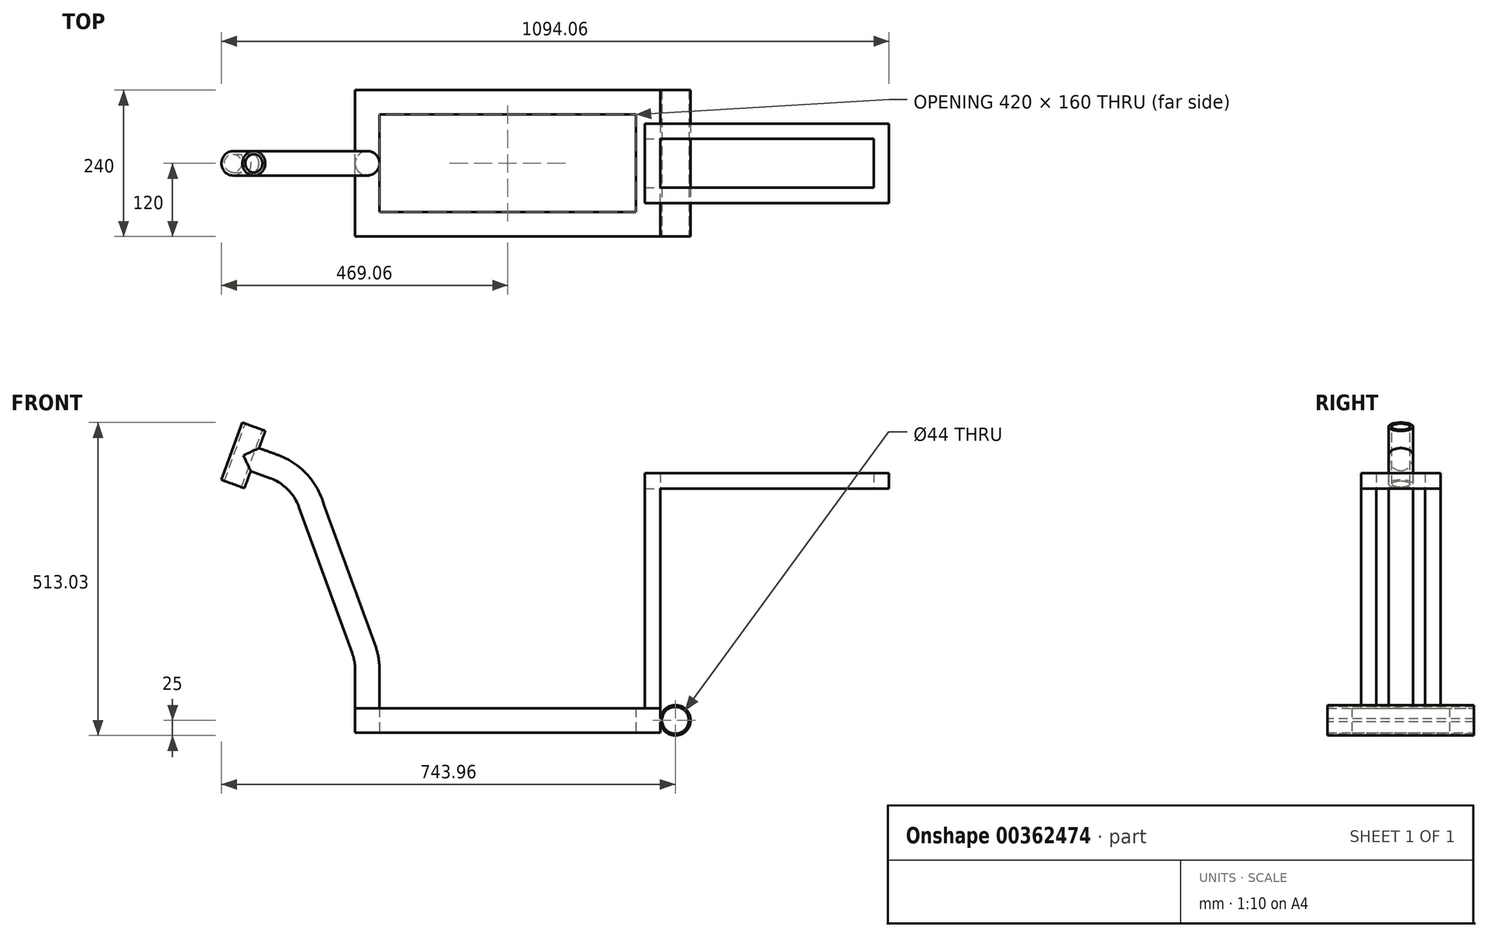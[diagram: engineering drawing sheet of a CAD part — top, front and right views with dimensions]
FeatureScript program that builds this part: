
annotation { "Feature Type Name" : "Feature", "Feature Type Description" : "" }
export const myFeature = defineFeature(function(context is Context, id is Id, definition is map)
    precondition{}
    {
        {
            var Q0;
            Q0=qCreatedBy(makeId("Top.planeOp"),FACE);
            var sketch = newSketch(context, id + "F0", { "sketchPlane" : qUnion([Q0])});
            skLineSegment(sketch, "E0.bottom", {"start": v(0, 0) * mm, "end": v(500, 0) * mm});
            skLineSegment(sketch, "E0.top", {"start": v(0, 240) * mm, "end": v(500, 240) * mm});
            skLineSegment(sketch, "E0.left", {"start": v(0, 0) * mm, "end": v(0, 240) * mm});
            skLineSegment(sketch, "E0.right", {"start": v(500, 0) * mm, "end": v(500, 240) * mm});
            skLineSegment(sketch, "E1.0", {"start": v(40, 40) * mm, "end": v(40, 200) * mm});
            skLineSegment(sketch, "E1.1", {"start": v(40, 40) * mm, "end": v(460, 40) * mm});
            skLineSegment(sketch, "E1.2", {"start": v(460, 40) * mm, "end": v(460, 200) * mm});
            skLineSegment(sketch, "E1.3", {"start": v(40, 200) * mm, "end": v(460, 200) * mm});
            skSolve(sketch);
        }
        {
            var Q0;
            Q0 = qSketchRegion(id + "F0", true);
            extrude(context, id + "F1", {"entities" : qUnion([Q0]), "depth" : 40 * mm, "offsetDistance" : 25 * mm});
        }
        {
            var Q0;
            Q0=makeQuery(id+"F1.opExtrude","SWEPT_FACE",FACE,{"disambiguationData":[OSD([sQuery(id+"F0.wireOp",EDGE,"E0.right")])]});
            var sketch = newSketch(context, id + "F2", { "sketchPlane" : qUnion([Q0])});
            skLineSegment(sketch, "E2.bottom", {"start": v(55, 40) * mm, "end": v(80, 40) * mm});
            skLineSegment(sketch, "E2.top", {"start": v(55, 400) * mm, "end": v(80, 400) * mm});
            skLineSegment(sketch, "E2.left", {"start": v(55, 40) * mm, "end": v(55, 400) * mm});
            skLineSegment(sketch, "E2.right", {"start": v(80, 40) * mm, "end": v(80, 400) * mm});
            skLineSegment(sketch, "E3", {"start": v(120, 40) * mm, "end": v(120, 0) * mm, "construction": true});
            skLineSegment(sketch, "E4.MirrorCS", {"start": v(185, 40) * mm, "end": v(185, 400) * mm});
            skLineSegment(sketch, "E5.MirrorCS", {"start": v(185, 400) * mm, "end": v(160, 400) * mm});
            skLineSegment(sketch, "E6.MirrorCS", {"start": v(160, 40) * mm, "end": v(160, 400) * mm});
            skLineSegment(sketch, "E7.MirrorCS", {"start": v(185, 40) * mm, "end": v(160, 40) * mm});
            skSolve(sketch);
        }
        {
            var Q0;
            Q0 = qSketchRegion(id + "F2", true);
            extrude(context, id + "F3", {"entities" : qUnion([Q0]), "operationType" : NewBodyOperationType.ADD, "oppositeDirection" : true, "depth" : 25 * mm, "offsetDistance" : 25 * mm});
        }
        {
            var Q0;
            Q0=makeQuery(id+"F3.opExtrude","SWEPT_FACE",FACE,{"disambiguationData":[OSD([sQuery(id+"F2.wireOp",EDGE,"E2.top")])]});
            var sketch = newSketch(context, id + "F4", { "sketchPlane" : qUnion([Q0])});
            skLineSegment(sketch, "E8.bottom", {"start": v(475, 55) * mm, "end": v(875, 55) * mm});
            skLineSegment(sketch, "E8.top", {"start": v(475, 185) * mm, "end": v(875, 185) * mm});
            skLineSegment(sketch, "E8.left", {"start": v(475, 55) * mm, "end": v(475, 185) * mm});
            skLineSegment(sketch, "E8.right", {"start": v(875, 55) * mm, "end": v(875, 185) * mm});
            skLineSegment(sketch, "E9.0", {"start": v(500, 160) * mm, "end": v(850, 160) * mm});
            skLineSegment(sketch, "E9.1", {"start": v(500, 80) * mm, "end": v(500, 160) * mm});
            skLineSegment(sketch, "E9.2", {"start": v(500, 80) * mm, "end": v(850, 80) * mm});
            skLineSegment(sketch, "E9.3", {"start": v(850, 80) * mm, "end": v(850, 160) * mm});
            skSolve(sketch);
        }
        {
            var Q0;
            Q0 = qSketchRegion(id + "F4", true);
            extrude(context, id + "F5", {"entities" : qUnion([Q0]), "operationType" : NewBodyOperationType.ADD, "depth" : 25 * mm});
        }
        {
            var Q0;
            Q0=qCreatedBy(makeId("Front.planeOp"),FACE);
            var sketch = newSketch(context, id + "F6", { "sketchPlane" : qUnion([Q0])});
            skCircle(sketch, "E10", {"center": v(524.9, 20) * mm, "radius": 25 * mm});
            skCircle(sketch, "E11.0", {"center": v(524.9, 20) * mm, "radius": 22 * mm});
            skSolve(sketch);
        }
        {
            var Q0;
            Q0 = qSketchRegion(id + "F6", true);
            extrude(context, id + "F7", {"entities" : qUnion([Q0]), "operationType" : NewBodyOperationType.ADD, "oppositeDirection" : true, "depth" : 240 * mm});
        }
        {
            var Q0;
            Q0=qCreatedBy(makeId("Front.planeOp"),FACE);
            var Q1;
            Q1=makeQuery(id+"F1.opExtrude","SWEPT_FACE",FACE,{"disambiguationData":[OSD([sQuery(id+"F0.wireOp",EDGE,"E0.top")])]});
            cPlane(context, id + "F8", {"entities" : qUnion([Q0, Q1]), "cplaneType" : CPlaneType.MID_PLANE, "offset" : 25 * mm, "width" : 150 * mm, "height" : 150 * mm});
        }
        {
            var Q0;
            Q0=qCreatedBy(id+"F8.planeOp",FACE);
            var sketch = newSketch(context, id + "F9", { "sketchPlane" : qUnion([Q0])});
            skLineSegment(sketch, "E12", {"start": v(20, 20) * mm, "end": v(20, 102.37) * mm});
            skLineSegment(sketch, "E13", {"start": v(13.97, 136.57) * mm, "end": v(-73.24, 376.18) * mm});
            skPoint(sketch, "E14.visualSharp", {"position": v(20, 120) * mm});
            skArc(sketch, "E15.filletArc", {"start": v(20, 102.37) * mm, "mid": v(18.48, 119.73) * mm, "end": v(13.97, 136.57) * mm});
            skLineSegment(sketch, "E16", {"start": v(-133, 435.95) * mm, "end": v(-183.16, 454.2) * mm});
            skPoint(sketch, "E17.visualSharp", {"position": v(-89.2, 420) * mm});
            skArc(sketch, "E17.filletArc", {"start": v(-73.24, 376.18) * mm, "mid": v(-96.5, 412.7) * mm, "end": v(-133, 435.95) * mm});
            skSolve(sketch);
        }
        {
            var Q0;
            Q0=sQuery(id+"F9.wireOp",VERTEX,"E12.start");
            var Q1;
            Q1=sQuery(id+"F9.wireOp",EDGE,"E12");
            cPlane(context, id + "F10", {"entities" : qUnion([Q0, Q1]), "cplaneType" : CPlaneType.LINE_POINT, "offset" : 25 * mm, "width" : 150 * mm, "height" : 150 * mm});
        }
        {
            var Q0;
            Q0=qCreatedBy(id+"F10.planeOp",FACE);
            var sketch = newSketch(context, id + "F11", { "sketchPlane" : qUnion([Q0])});
            skCircle(sketch, "E18", {"center": v(20, 120) * mm, "radius": 20 * mm});
            skSolve(sketch);
        }
        {
            var Q0;
            Q0 = qSketchRegion(id + "F11", true);
            var Q1;
            Q1 = qConstructionFilter(qBodyType(qCreatedBy(id + "F9" ,EDGE), BodyType.WIRE), ConstructionObject.NO);
            sweep(context, id + "F12", {"operationType" : NewBodyOperationType.ADD, "profiles" : qUnion([Q0]), "path" : qUnion([Q1])});
        }
        {
            var Q0;
            Q0=makeQuery(id+"F12.opSweep","CAP_FACE",FACE,{"disambiguationData":[OSD([sQuery(id+"F9.wireOp",VERTEX,"E16.end"),sQuery(id+"F11.wireOp",EDGE,"E18")])],"isStart":false});
            var sketch = newSketch(context, id + "F13", { "sketchPlane" : qUnion([Q0])});
            skLineSegment(sketch, "E19.bottom", {"start": v(-140, 414.17) * mm, "end": v(-120, 414.17) * mm});
            skLineSegment(sketch, "E19.top", {"start": v(-140, 314.17) * mm, "end": v(-120, 314.17) * mm});
            skLineSegment(sketch, "E19.left", {"start": v(-140, 414.17) * mm, "end": v(-140, 314.17) * mm});
            skPoint(sketch, "E19.middle", {"position": v(-120, 364.17) * mm});
            skLineSegment(sketch, "E20", {"start": v(-120, 414.17) * mm, "end": v(-120, 314.17) * mm});
            skPoint(sketch, "E19.right.start.orphan", {"position": v(-100, 414.17) * mm});
            skPoint(sketch, "E21.orphan", {"position": v(-100, 314.17) * mm});
            skSolve(sketch);
        }
        {
            var Q0;
            Q0 = qSketchRegion(id + "F13", true);
            var Q1;
            Q1=sQuery(id+"F13.wireOp",EDGE,"E20");
            revolve(context, id + "F14", {"operationType" : NewBodyOperationType.ADD, "entities" : qUnion([Q0]), "axis" : qUnion([Q1]), "revolveType" : RevolveType.FULL});
        }
        {
            var Q0;
            Q0=makeQuery(id+"F14.opRevolve","SWEPT_FACE",FACE,{"disambiguationData":[OSD([sQuery(id+"F13.wireOp",EDGE,"E19.bottom")])]});
            var sketch = newSketch(context, id + "F15", { "sketchPlane" : qUnion([Q0])});
            skCircle(sketch, "E22", {"center": v(-327.46, 120) * mm, "radius": 15 * mm});
            skSolve(sketch);
        }
        {
            var Q0;
            Q0 = qSketchRegion(id + "F15", true);
            extrude(context, id + "F16", {"entities" : qUnion([Q0]), "operationType" : NewBodyOperationType.REMOVE, "endBound" : BoundingType.THROUGH_ALL, "oppositeDirection" : true, "depth" : 25 * mm});
        }
    });
